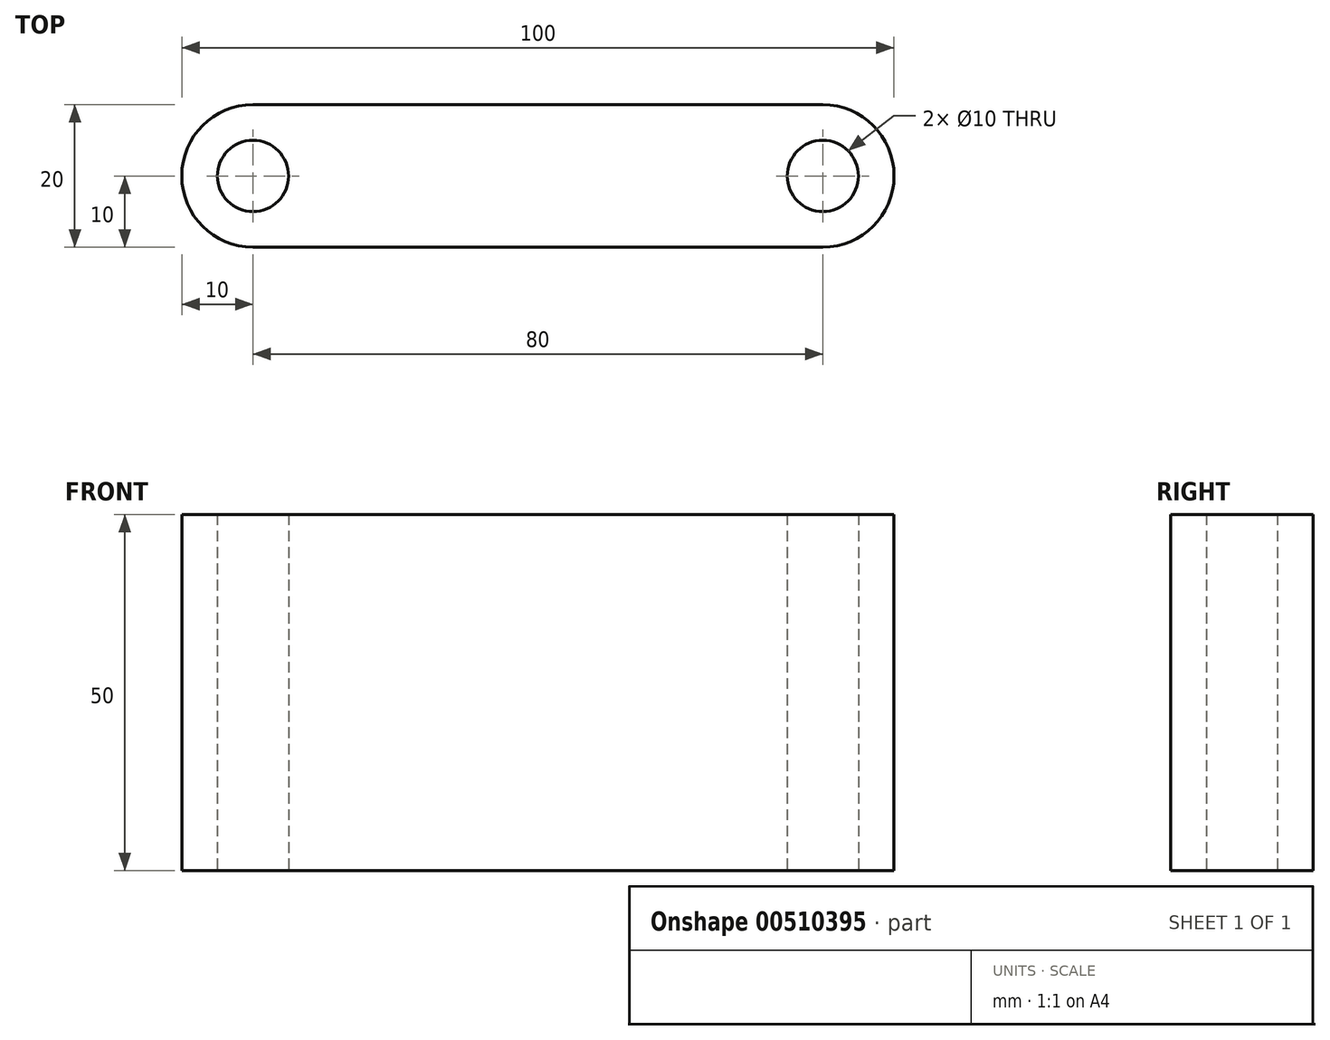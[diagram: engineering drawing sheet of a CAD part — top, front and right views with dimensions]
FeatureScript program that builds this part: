
annotation { "Feature Type Name" : "Feature", "Feature Type Description" : "" }
export const myFeature = defineFeature(function(context is Context, id is Id, definition is map)
    precondition{}
    {
        {
            var Q0;
            Q0=qCreatedBy(makeId("Top.planeOp"),FACE);
            var sketch = newSketch(context, id + "F0", { "sketchPlane" : qUnion([Q0])});
            skLineSegment(sketch, "E0.bottom", {"start": v(40, 10) * mm, "end": v(-40, 10) * mm});
            skLineSegment(sketch, "E0.top", {"start": v(40, -10) * mm, "end": v(-40, -10) * mm});
            skPoint(sketch, "E0.middle", {"position": v(0, 0) * mm});
            skArc(sketch, "E1", {"start": v(-40, 10) * mm, "mid": v(-50, 0) * mm, "end": v(-40, -10) * mm});
            skCircle(sketch, "E2", {"center": v(-40, 0) * mm, "radius": 5 * mm});
            skLineSegment(sketch, "E3", {"start": v(0, -10) * mm, "end": v(0, 64.94) * mm, "construction": true});
            skPoint(sketch, "E3.endSnap0", {"position": v(0, -10) * mm});
            skArc(sketch, "E4.MirrorCS", {"start": v(40, 10) * mm, "mid": v(50, 0) * mm, "end": v(40, -10) * mm});
            skCircle(sketch, "E5.MirrorC", {"center": v(40, 0) * mm, "radius": 5 * mm});
            skSolve(sketch);
        }
        {
            var Q0;
            Q0=makeQuery(id+"F0.imprint","IMPRINT",FACE,{"disambiguationData":[TD([[makeQuery(id+"F0.imprint","IMPRINT",EDGE,{"derivedFrom":sQuery(id+"F0.wireOp",EDGE,"E0.bottom")}),1.0]])]});
            extrude(context, id + "F1", {"entities" : qUnion([Q0]), "endBound" : BoundingType.SYMMETRIC, "depth" : 15 * mm});
        }
        {
            var Q0;
            Q0=makeQuery(id+"F1.opExtrude","CAP_FACE",FACE,{"disambiguationData":[OSD([sQuery(id+"F0.wireOp",EDGE,"E0.bottom"),sQuery(id+"F0.wireOp",EDGE,"E0.top"),sQuery(id+"F0.wireOp",EDGE,"E1"),sQuery(id+"F0.wireOp",EDGE,"E2"),sQuery(id+"F0.wireOp",EDGE,"E4.MirrorCS"),sQuery(id+"F0.wireOp",EDGE,"E5.MirrorC")])],"isStart":false});
            var sketch = newSketch(context, id + "F2", { "sketchPlane" : qUnion([Q0])});
            skCircle(sketch, "E6", {"center": v(40, 0) * mm, "radius": 5 * mm});
            skSolve(sketch);
        }
        {
            var Q0;
            Q0=makeQuery(id+"F2.imprint","IMPRINT",FACE,{"disambiguationData":[TD([[makeQuery(id+"F2.imprint","IMPRINT",EDGE,{"derivedFrom":sQuery(id+"F2.wireOp",EDGE,"E6")}),-1.0]])]});
            extrude(context, id + "F3", {"entities" : qUnion([Q0]), "operationType" : NewBodyOperationType.ADD, "endBound" : BoundingType.SYMMETRIC, "depth" : 70 * mm});
        }
        {
            var Q0;
            Q0=makeQuery(id+"F3.opExtrude","CAP_FACE",FACE,{"disambiguationData":[OSD([sQuery(id+"F2.wireOp",EDGE,"E6")])],"isStart":true});
            var sketch = newSketch(context, id + "F4", { "sketchPlane" : qUnion([Q0])});
            skCircle(sketch, "E7", {"center": v(40, 0) * mm, "radius": 5 * mm});
            skSolve(sketch);
        }
        {
            var Q0;
            Q0=makeQuery(id+"F4.imprint","IMPRINT",FACE,{"disambiguationData":[TD([[makeQuery(id+"F4.imprint","IMPRINT",EDGE,{"derivedFrom":sQuery(id+"F4.wireOp",EDGE,"E7")}),1.0]])]});
            extrude(context, id + "F5", {"entities" : qUnion([Q0]), "operationType" : NewBodyOperationType.REMOVE, "oppositeDirection" : true, "depth" : 20 * mm});
        }
    });
